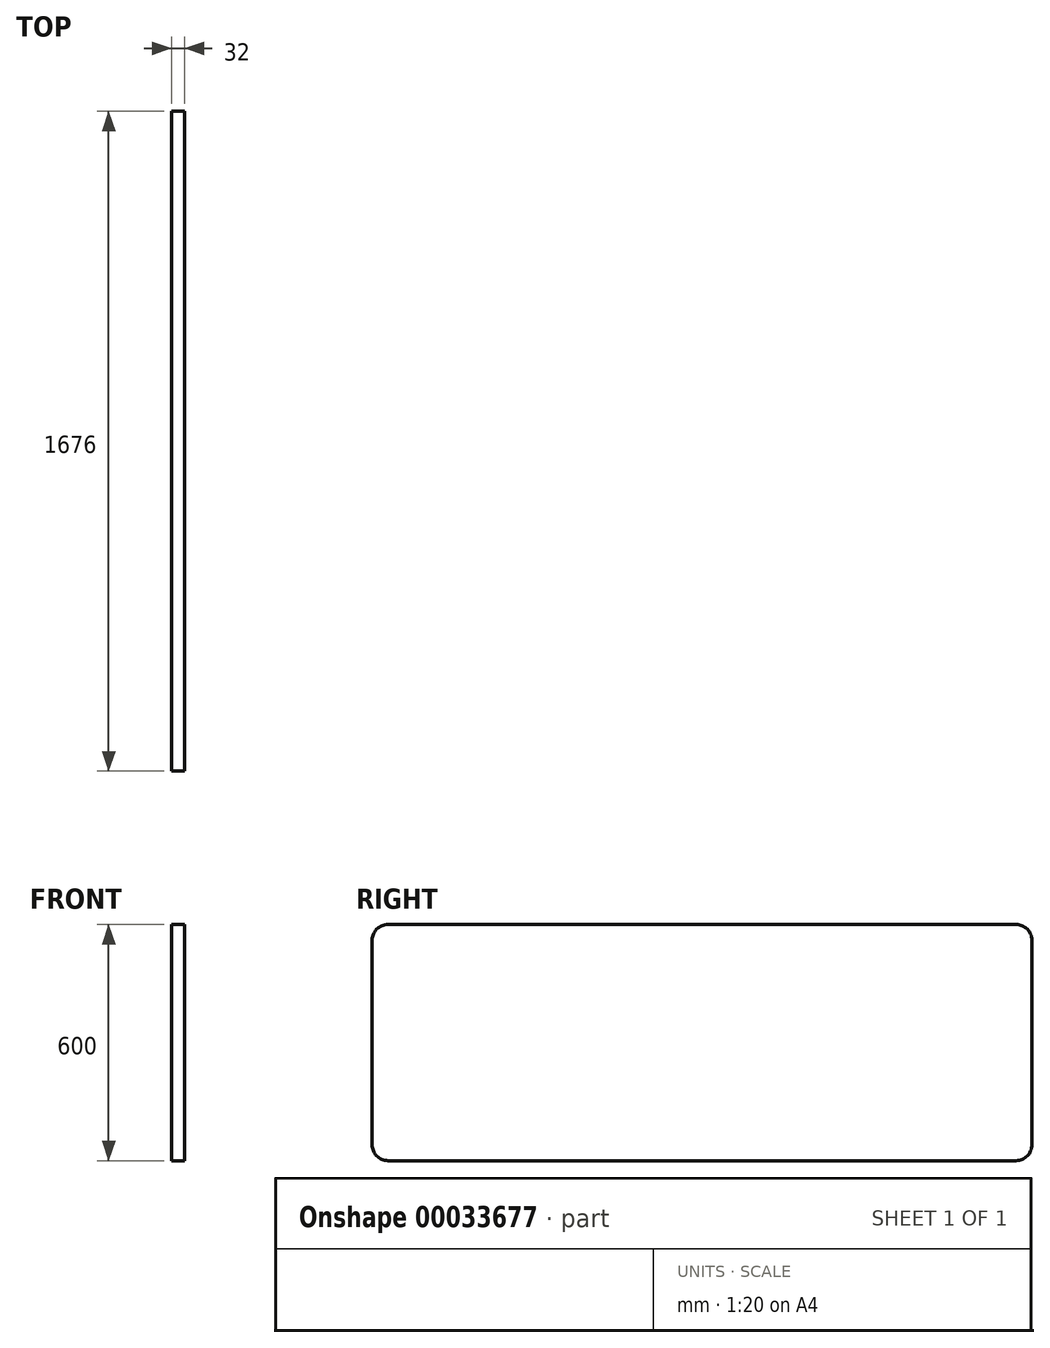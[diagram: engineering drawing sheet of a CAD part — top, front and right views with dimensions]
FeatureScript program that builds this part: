
annotation { "Feature Type Name" : "Feature", "Feature Type Description" : "" }
export const myFeature = defineFeature(function(context is Context, id is Id, definition is map)
    precondition{}
    {
        {
            var Q0;
            Q0=qCreatedBy(makeId("Right.planeOp"),FACE);
            var sketch = newSketch(context, id + "F0", { "sketchPlane" : qUnion([Q0])});
            skLineSegment(sketch, "E0.bottom", {"start": v(0, 0) * mm, "end": v(1676, 0) * mm});
            skLineSegment(sketch, "E0.top", {"start": v(0, 600) * mm, "end": v(1676, 600) * mm});
            skLineSegment(sketch, "E0.left", {"start": v(0, 0) * mm, "end": v(0, 600) * mm});
            skLineSegment(sketch, "E0.right", {"start": v(1676, 0) * mm, "end": v(1676, 600) * mm});
            skSolve(sketch);
        }
        {
            var Q0;
            Q0 = qSketchRegion(id + "F0", true);
            extrude(context, id + "F1", {"entities" : qUnion([Q0]), "depth" : 32 * mm});
        }
        {
            var Q0;
            Q0=makeQuery(id+"F1.opExtrude","SWEPT_EDGE",EDGE,{"disambiguationData":[OSD([sQuery(id+"F0.wireOp",EDGE,"E0.top"),sQuery(id+"F0.wireOp",EDGE,"E0.left")])]});
            var Q1;
            Q1=makeQuery(id+"F1.opExtrude","SWEPT_EDGE",EDGE,{"disambiguationData":[OSD([sQuery(id+"F0.wireOp",EDGE,"E0.bottom"),sQuery(id+"F0.wireOp",EDGE,"E0.left")])]});
            var Q2;
            Q2=makeQuery(id+"F1.opExtrude","SWEPT_EDGE",EDGE,{"disambiguationData":[OSD([sQuery(id+"F0.wireOp",EDGE,"E0.bottom"),sQuery(id+"F0.wireOp",EDGE,"E0.right")])]});
            var Q3;
            Q3=makeQuery(id+"F1.opExtrude","SWEPT_EDGE",EDGE,{"disambiguationData":[OSD([sQuery(id+"F0.wireOp",EDGE,"E0.top"),sQuery(id+"F0.wireOp",EDGE,"E0.right")])]});
            fillet(context, id + "F2", {"entities" : qUnion([Q0, Q1, Q2, Q3]), "radius" : 40 * mm, "tangentPropagation" : true, "allowEdgeOverflow" : false});
        }
    });
